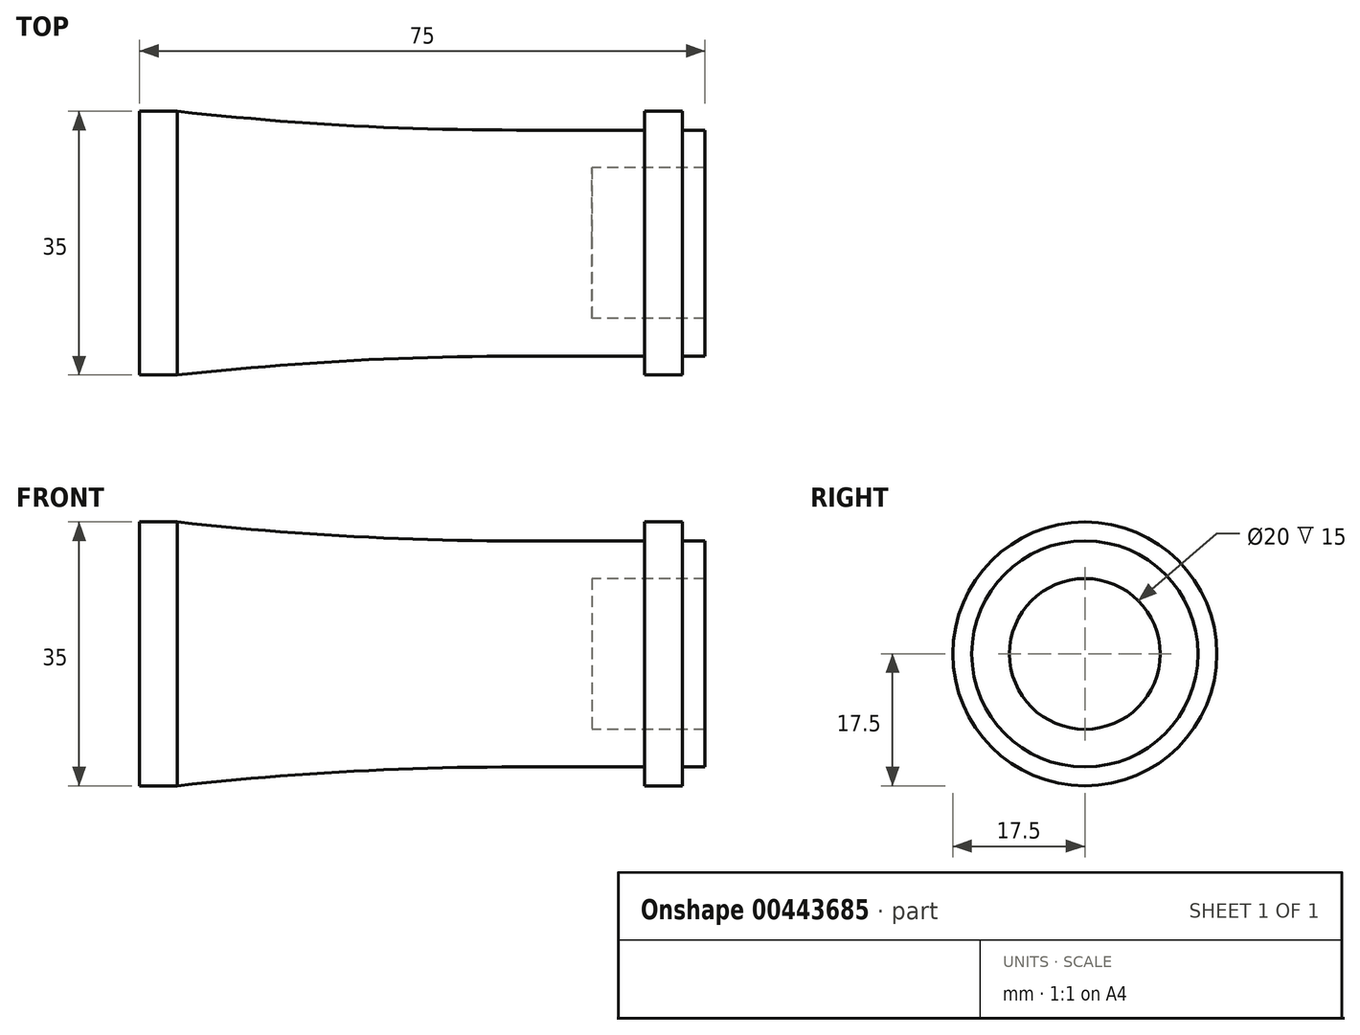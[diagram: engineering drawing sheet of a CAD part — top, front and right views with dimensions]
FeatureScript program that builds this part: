
annotation { "Feature Type Name" : "Feature", "Feature Type Description" : "" }
export const myFeature = defineFeature(function(context is Context, id is Id, definition is map)
    precondition{}
    {
        {
            var Q0;
            Q0=qCreatedBy(makeId("Front.planeOp"),FACE);
            var sketch = newSketch(context, id + "F0", { "sketchPlane" : qUnion([Q0])});
            skLineSegment(sketch, "E0", {"start": v(0, 0) * mm, "end": v(60, 0) * mm});
            skLineSegment(sketch, "E1", {"start": v(60, 0) * mm, "end": v(60, 10) * mm});
            skLineSegment(sketch, "E2", {"start": v(60, 10) * mm, "end": v(75, 10) * mm});
            skLineSegment(sketch, "E3", {"start": v(75, 10) * mm, "end": v(75, 15) * mm});
            skLineSegment(sketch, "E4", {"start": v(75, 15) * mm, "end": v(72, 15) * mm});
            skLineSegment(sketch, "E5", {"start": v(72, 15) * mm, "end": v(72, 17.5) * mm});
            skLineSegment(sketch, "E6", {"start": v(72, 17.5) * mm, "end": v(67, 17.5) * mm});
            skLineSegment(sketch, "E7", {"start": v(67, 17.5) * mm, "end": v(67, 15) * mm});
            skLineSegment(sketch, "E8", {"start": v(67, 15) * mm, "end": v(50, 15) * mm});
            skLineSegment(sketch, "E9", {"start": v(0, 0) * mm, "end": v(0, 17.5) * mm});
            skLineSegment(sketch, "E10", {"start": v(0, 17.5) * mm, "end": v(5, 17.5) * mm});
            skArc(sketch, "E11", {"start": v(5, 17.5) * mm, "mid": v(27.47, 15.63) * mm, "end": v(50, 15) * mm});
            skSolve(sketch);
        }
        {
            var Q0;
            Q0 = qSketchRegion(id + "F0", true);
            var Q1;
            Q1=sQuery(id+"F0.wireOp",EDGE,"E0");
            revolve(context, id + "F1", {"entities" : qUnion([Q0]), "axis" : qUnion([Q1]), "revolveType" : RevolveType.FULL});
        }
    });
